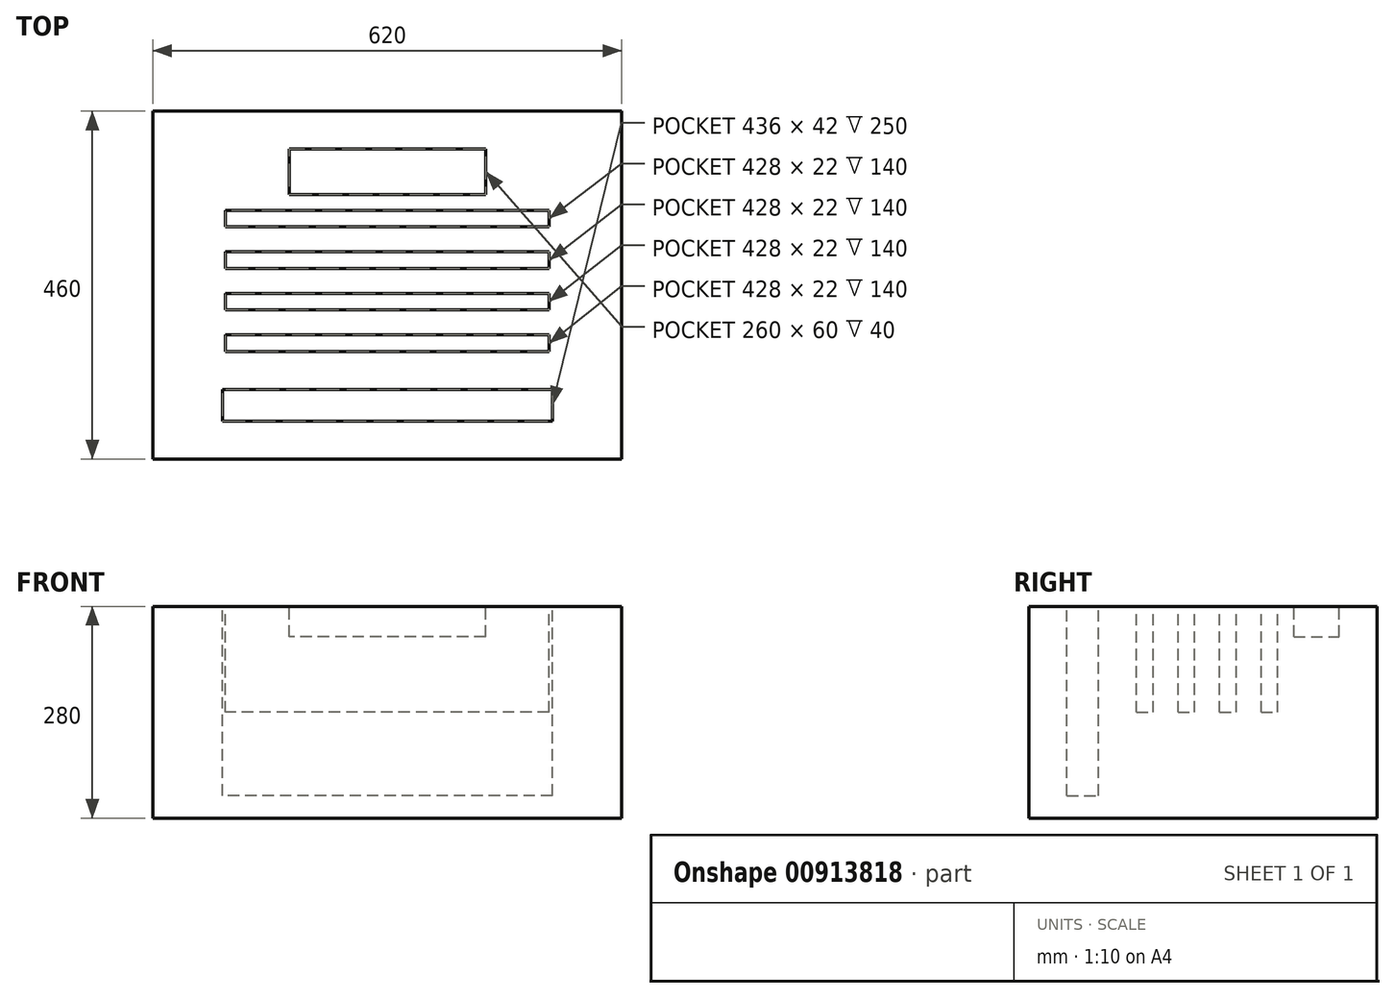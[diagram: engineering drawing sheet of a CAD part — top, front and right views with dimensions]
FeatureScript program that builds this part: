
annotation { "Feature Type Name" : "Feature", "Feature Type Description" : "" }
export const myFeature = defineFeature(function(context is Context, id is Id, definition is map)
    precondition{}
    {
        {
            var Q0;
            Q0=qCreatedBy(makeId("Top.planeOp"),FACE);
            var sketch = newSketch(context, id + "F0", { "sketchPlane" : qUnion([Q0])});
            skLineSegment(sketch, "E0.bottom", {"start": v(310.34, -142) * mm, "end": v(-309.66, -142) * mm});
            skLineSegment(sketch, "E0.top", {"start": v(310.34, 318) * mm, "end": v(-309.66, 318) * mm});
            skLineSegment(sketch, "E0.left", {"start": v(310.34, -142) * mm, "end": v(310.34, 318) * mm});
            skLineSegment(sketch, "E0.right", {"start": v(-309.66, -142) * mm, "end": v(-309.66, 318) * mm});
            skLineSegment(sketch, "E1.bottom", {"start": v(218.34, -92) * mm, "end": v(-217.66, -92) * mm});
            skLineSegment(sketch, "E1.top", {"start": v(218.34, -50) * mm, "end": v(-217.66, -50) * mm});
            skLineSegment(sketch, "E1.left", {"start": v(218.34, -92) * mm, "end": v(218.34, -50) * mm});
            skLineSegment(sketch, "E1.right", {"start": v(-217.66, -92) * mm, "end": v(-217.66, -50) * mm});
            skPoint(sketch, "E1.middle", {"position": v(0, 0) * mm});
            skLineSegment(sketch, "E2.direction1", {"start": v(-217.66, -92) * mm, "end": v(-182.5, -92) * mm, "construction": true});
            skLineSegment(sketch, "E2.direction2", {"start": v(-217.66, -92) * mm, "end": v(-217.66, -20) * mm, "construction": true});
            skLineSegment(sketch, "E3.bottom", {"start": v(214, 0) * mm, "end": v(-214, 0) * mm});
            skLineSegment(sketch, "E3.top", {"start": v(214, 22) * mm, "end": v(-214, 22) * mm});
            skLineSegment(sketch, "E3.left", {"start": v(214, 0) * mm, "end": v(214, 22) * mm});
            skLineSegment(sketch, "E3.right", {"start": v(-214, 0) * mm, "end": v(-214, 22) * mm});
            skPoint(sketch, "E3.middle", {"position": v(0, 11) * mm});
            skLineSegment(sketch, "E4.0.1.0", {"start": v(-214, 55) * mm, "end": v(-214, 77) * mm});
            skLineSegment(sketch, "E4.0.1.1", {"start": v(214, 55) * mm, "end": v(-214, 55) * mm});
            skLineSegment(sketch, "E4.0.1.2", {"start": v(214, 77) * mm, "end": v(-214, 77) * mm});
            skLineSegment(sketch, "E4.0.1.3", {"start": v(214, 55) * mm, "end": v(214, 77) * mm});
            skLineSegment(sketch, "E4.direction1", {"start": v(-214, 0) * mm, "end": v(-189, 0) * mm, "construction": true});
            skLineSegment(sketch, "E4.direction2", {"start": v(-214, 0) * mm, "end": v(-214, 55) * mm, "construction": true});
            skLineSegment(sketch, "E5.0.0.2", {"start": v(-214, 110) * mm, "end": v(-214, 132) * mm});
            skLineSegment(sketch, "E5.3.0.2", {"start": v(214, 110) * mm, "end": v(-214, 110) * mm});
            skLineSegment(sketch, "E5.6.0.2", {"start": v(214, 132) * mm, "end": v(-214, 132) * mm});
            skLineSegment(sketch, "E5.9.0.2", {"start": v(214, 110) * mm, "end": v(214, 132) * mm});
            skLineSegment(sketch, "E5.0.0.3", {"start": v(-214, 165) * mm, "end": v(-214, 187) * mm});
            skLineSegment(sketch, "E5.3.0.3", {"start": v(214, 165) * mm, "end": v(-214, 165) * mm});
            skLineSegment(sketch, "E5.6.0.3", {"start": v(214, 187) * mm, "end": v(-214, 187) * mm});
            skLineSegment(sketch, "E5.9.0.3", {"start": v(214, 165) * mm, "end": v(214, 187) * mm});
            skSolve(sketch);
        }
        {
            var Q0;
            Q0=makeQuery(id+"F0.imprint","IMPRINT",FACE,{"disambiguationData":[TD([[makeQuery(id+"F0.imprint","IMPRINT",EDGE,{"derivedFrom":sQuery(id+"F0.wireOp",EDGE,"E0.bottom")}),-1.0]])]});
            var Q1;
            Q1=makeQuery(id+"F0.imprint","IMPRINT",FACE,{"disambiguationData":[TD([[makeQuery(id+"F0.imprint","IMPRINT",EDGE,{"derivedFrom":sQuery(id+"F0.wireOp",EDGE,"E2.0.2.0")}),1.0]])]});
            var Q2;
            Q2=makeQuery(id+"F0.imprint","IMPRINT",FACE,{"disambiguationData":[TD([[makeQuery(id+"F0.imprint","IMPRINT",EDGE,{"derivedFrom":sQuery(id+"F0.wireOp",EDGE,"E2.0.1.0")}),1.0]])]});
            var Q3;
            Q3=makeQuery(id+"F0.imprint","IMPRINT",FACE,{"disambiguationData":[TD([[makeQuery(id+"F0.imprint","IMPRINT",EDGE,{"derivedFrom":sQuery(id+"F0.wireOp",EDGE,"E1.bottom")}),-1.0]])]});
            var Q4;
            Q4=makeQuery(id+"F0.imprint","IMPRINT",FACE,{"disambiguationData":[TD([[makeQuery(id+"F0.imprint","IMPRINT",EDGE,{"derivedFrom":sQuery(id+"F0.wireOp",EDGE,"E3.bottom")}),-1.0]])]});
            var Q5;
            Q5=makeQuery(id+"F0.imprint","IMPRINT",FACE,{"disambiguationData":[TD([[makeQuery(id+"F0.imprint","IMPRINT",EDGE,{"derivedFrom":sQuery(id+"F0.wireOp",EDGE,"E4.0.1.0")}),-1.0]])]});
            var Q6;
            Q6=makeQuery(id+"F0.imprint","IMPRINT",FACE,{"disambiguationData":[TD([[makeQuery(id+"F0.imprint","IMPRINT",EDGE,{"derivedFrom":sQuery(id+"F0.wireOp",EDGE,"E4.0.2.0")}),-1.0]])]});
            var Q7;
            Q7=makeQuery(id+"F0.imprint","IMPRINT",FACE,{"disambiguationData":[TD([[makeQuery(id+"F0.imprint","IMPRINT",EDGE,{"derivedFrom":sQuery(id+"F0.wireOp",EDGE,"E4.0.3.0")}),-1.0]])]});
            var Q8;
            Q8=makeQuery(id+"F0.imprint","IMPRINT",FACE,{"disambiguationData":[TD([[makeQuery(id+"F0.imprint","IMPRINT",EDGE,{"derivedFrom":sQuery(id+"F0.wireOp",EDGE,"E4.0.4.0")}),-1.0]])]});
            var Q9;
            Q9=makeQuery(id+"F0.imprint","IMPRINT",FACE,{"disambiguationData":[TD([[makeQuery(id+"F0.imprint","IMPRINT",EDGE,{"derivedFrom":sQuery(id+"F0.wireOp",EDGE,"E4.0.5.0")}),-1.0]])]});
            var Q10;
            Q10=makeQuery(id+"F0.imprint","IMPRINT",FACE,{"disambiguationData":[TD([[makeQuery(id+"F0.imprint","IMPRINT",EDGE,{"derivedFrom":sQuery(id+"F0.wireOp",EDGE,"E5.0.0.2")}),-1.0]])]});
            var Q11;
            Q11=makeQuery(id+"F0.imprint","IMPRINT",FACE,{"disambiguationData":[TD([[makeQuery(id+"F0.imprint","IMPRINT",EDGE,{"derivedFrom":sQuery(id+"F0.wireOp",EDGE,"E5.0.0.3")}),-1.0]])]});
            extrude(context, id + "F1", {"entities" : qUnion([Q0, Q1, Q2, Q3, Q4, Q5, Q6, Q7, Q8, Q9, Q10, Q11]), "oppositeDirection" : true, "depth" : 280 * mm, "offsetDistance" : 25 * mm});
        }
        {
            var Q0;
            Q0=makeQuery(id+"F0.imprint","IMPRINT",FACE,{"disambiguationData":[TD([[makeQuery(id+"F0.imprint","IMPRINT",EDGE,{"derivedFrom":sQuery(id+"F0.wireOp",EDGE,"E2.0.1.0")}),1.0]])]});
            var Q1;
            Q1=makeQuery(id+"F0.imprint","IMPRINT",FACE,{"disambiguationData":[TD([[makeQuery(id+"F0.imprint","IMPRINT",EDGE,{"derivedFrom":sQuery(id+"F0.wireOp",EDGE,"E1.bottom")}),-1.0]])]});
            extrude(context, id + "F2", {"entities" : qUnion([Q0, Q1]), "operationType" : NewBodyOperationType.REMOVE, "oppositeDirection" : true, "depth" : 250 * mm, "offsetDistance" : 25 * mm});
        }
        {
            var Q0;
            Q0=makeQuery(id+"F0.imprint","IMPRINT",FACE,{"disambiguationData":[TD([[makeQuery(id+"F0.imprint","IMPRINT",EDGE,{"derivedFrom":sQuery(id+"F0.wireOp",EDGE,"E3.bottom")}),-1.0]])]});
            var Q1;
            Q1=makeQuery(id+"F0.imprint","IMPRINT",FACE,{"disambiguationData":[TD([[makeQuery(id+"F0.imprint","IMPRINT",EDGE,{"derivedFrom":sQuery(id+"F0.wireOp",EDGE,"E4.0.1.0")}),-1.0]])]});
            var Q2;
            Q2=makeQuery(id+"F0.imprint","IMPRINT",FACE,{"disambiguationData":[TD([[makeQuery(id+"F0.imprint","IMPRINT",EDGE,{"derivedFrom":sQuery(id+"F0.wireOp",EDGE,"E4.0.2.0")}),-1.0]])]});
            var Q3;
            Q3=makeQuery(id+"F0.imprint","IMPRINT",FACE,{"disambiguationData":[TD([[makeQuery(id+"F0.imprint","IMPRINT",EDGE,{"derivedFrom":sQuery(id+"F0.wireOp",EDGE,"E4.0.3.0")}),-1.0]])]});
            var Q4;
            Q4=makeQuery(id+"F0.imprint","IMPRINT",FACE,{"disambiguationData":[TD([[makeQuery(id+"F0.imprint","IMPRINT",EDGE,{"derivedFrom":sQuery(id+"F0.wireOp",EDGE,"E4.0.4.0")}),-1.0]])]});
            var Q5;
            Q5=makeQuery(id+"F0.imprint","IMPRINT",FACE,{"disambiguationData":[TD([[makeQuery(id+"F0.imprint","IMPRINT",EDGE,{"derivedFrom":sQuery(id+"F0.wireOp",EDGE,"E4.0.5.0")}),-1.0]])]});
            var Q6;
            Q6=makeQuery(id+"F0.imprint","IMPRINT",FACE,{"disambiguationData":[TD([[makeQuery(id+"F0.imprint","IMPRINT",EDGE,{"derivedFrom":sQuery(id+"F0.wireOp",EDGE,"E5.0.0.2")}),-1.0]])]});
            var Q7;
            Q7=makeQuery(id+"F0.imprint","IMPRINT",FACE,{"disambiguationData":[TD([[makeQuery(id+"F0.imprint","IMPRINT",EDGE,{"derivedFrom":sQuery(id+"F0.wireOp",EDGE,"E5.0.0.3")}),-1.0]])]});
            extrude(context, id + "F3", {"entities" : qUnion([Q0, Q1, Q2, Q3, Q4, Q5, Q6, Q7]), "operationType" : NewBodyOperationType.REMOVE, "oppositeDirection" : true, "depth" : 140 * mm, "offsetDistance" : 25 * mm});
        }
        {
            var Q0;
            Q0=makeQuery(id+"F1.opExtrude","CAP_FACE",FACE,{"disambiguationData":[OSD([sQuery(id+"F0.wireOp",EDGE,"E0.bottom"),sQuery(id+"F0.wireOp",EDGE,"E0.top"),sQuery(id+"F0.wireOp",EDGE,"E0.left"),sQuery(id+"F0.wireOp",EDGE,"E0.right")])],"isStart":true});
            var sketch = newSketch(context, id + "F4", { "sketchPlane" : qUnion([Q0])});
            skLineSegment(sketch, "E6.bottom", {"start": v(130.34, 208) * mm, "end": v(-129.66, 208) * mm});
            skLineSegment(sketch, "E6.top", {"start": v(130.34, 268) * mm, "end": v(-129.66, 268) * mm});
            skLineSegment(sketch, "E6.left", {"start": v(130.34, 208) * mm, "end": v(130.34, 268) * mm});
            skLineSegment(sketch, "E6.right", {"start": v(-129.66, 208) * mm, "end": v(-129.66, 268) * mm});
            skPoint(sketch, "E6.middle", {"position": v(0.34, 238) * mm});
            skSolve(sketch);
        }
        {
            var Q0;
            Q0=makeQuery(id+"F4.imprint","IMPRINT",FACE,{"disambiguationData":[TD([[makeQuery(id+"F4.imprint","IMPRINT",EDGE,{"derivedFrom":sQuery(id+"F4.wireOp",EDGE,"E6.bottom")}),-1.0]])]});
            extrude(context, id + "F5", {"entities" : qUnion([Q0]), "operationType" : NewBodyOperationType.REMOVE, "oppositeDirection" : true, "depth" : 40 * mm, "offsetDistance" : 25 * mm});
        }
    });
